# Revit family: Showerhead-DXV-Percy-D35120770_Series
name_source: partatom
category: Plumbing Fixtures
revit_build: Autodesk Revit 2018 (Build: 20170223_1515(x64)
units: mm (PartAtom-declared; Revit-internal decimal feet)

## family parameters
Always vertical = No
Cut with Voids When Loaded = No
OmniClass Number = 23.45.05.14.17
OmniClass Title = Showers
Part Type = Normal
Room Calculation Point = No
Round Connector Dimension = Use Diameter
Shared = Yes
Work Plane-Based = Yes

## types (4) — shared parameters
Assembly Code = D2010710
CW Connection = No
CWFU = 3
CalGreen Compliant = Yes
Default Elevation = 0"
Description = DXV Modulus 7-1/2'' Showerhead
Diameter = 7 1/2"
Flow Rate = 1.8 gpm (6.8 L/min)
HW Connection = No
HWFU = 3
Height = 1 5/16"
IAPMO Compliance = Meets or Exceeds ASME A112.18.1/CSA B125.1, EPA WaterSense® Certified
Installation Type = Ceiling Mounted
Manufacturer = DXV
Price = Prices may vary. Please consult Manufacturer Representative for most up-to-date price list.
Product Documentation Link = https://dxv01.blob.core.windows.net
Product Page URL = https://www.dxv.com
Revised Date = 04/07/2022
Tempered Water Connection = Yes
Tempered Water Connection Diameter = 1/2"
URL = www.dxv.com
Vent Connection = No
WFU = 4
Waste Connection = No

## per-type parameters (varying)
| type | Finish | Material |
| D35120770.150 | Metal-DXV-150-Platinum Nickel | Metal-DXV-150-Platinum Nickel |
| D35120770.100 | Metal-DXV-100-Polished Chrome | Metal-DXV-100-Polished Chrome |
| D35120770.144 | Metal-DXV-144-Brushed Nickel | Metal-DXV-144-Brushed Nickel |
| D35120770.243 | Metal-DXV-243-Matte Black | Metal-DXV-243-Matte Black |

note: column(s) folded — value = type name in every type: Model

## geometry (parser evidence)
native form markers: Sweep x2
no freeform markers — native parametric forms only
